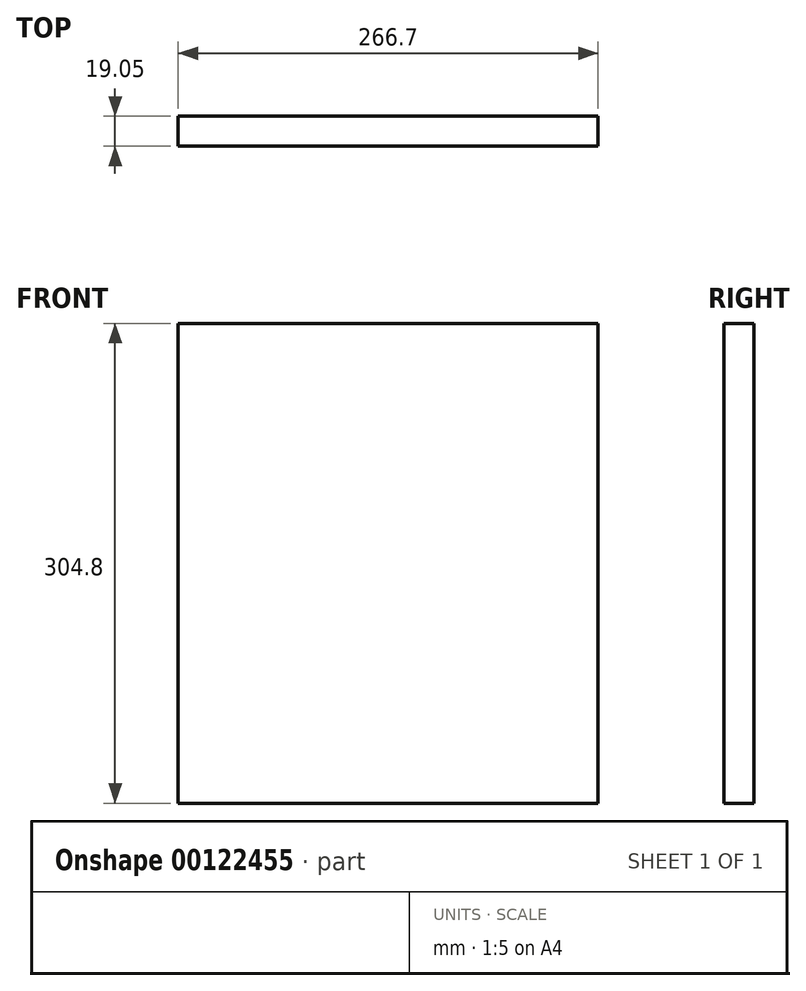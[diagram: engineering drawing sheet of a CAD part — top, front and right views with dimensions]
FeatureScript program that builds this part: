
annotation { "Feature Type Name" : "Feature", "Feature Type Description" : "" }
export const myFeature = defineFeature(function(context is Context, id is Id, definition is map)
    precondition{}
    {
        {
            var Q0;
            Q0=qCreatedBy(makeId("Front.planeOp"),FACE);
            var sketch = newSketch(context, id + "F0", { "sketchPlane" : qUnion([Q0])});
            skLineSegment(sketch, "E0.bottom", {"start": v(0, 0) * mm, "end": v(266.7, 0) * mm});
            skLineSegment(sketch, "E0.top", {"start": v(0, 304.8) * mm, "end": v(266.7, 304.8) * mm});
            skLineSegment(sketch, "E0.left", {"start": v(0, 0) * mm, "end": v(0, 304.8) * mm});
            skLineSegment(sketch, "E0.right", {"start": v(266.7, 0) * mm, "end": v(266.7, 304.8) * mm});
            skSolve(sketch);
        }
        {
            var Q0;
            Q0 = qSketchRegion(id + "F0", true);
            extrude(context, id + "F1", {"entities" : qUnion([Q0]), "depth" : 19.05 * mm});
        }
    });
